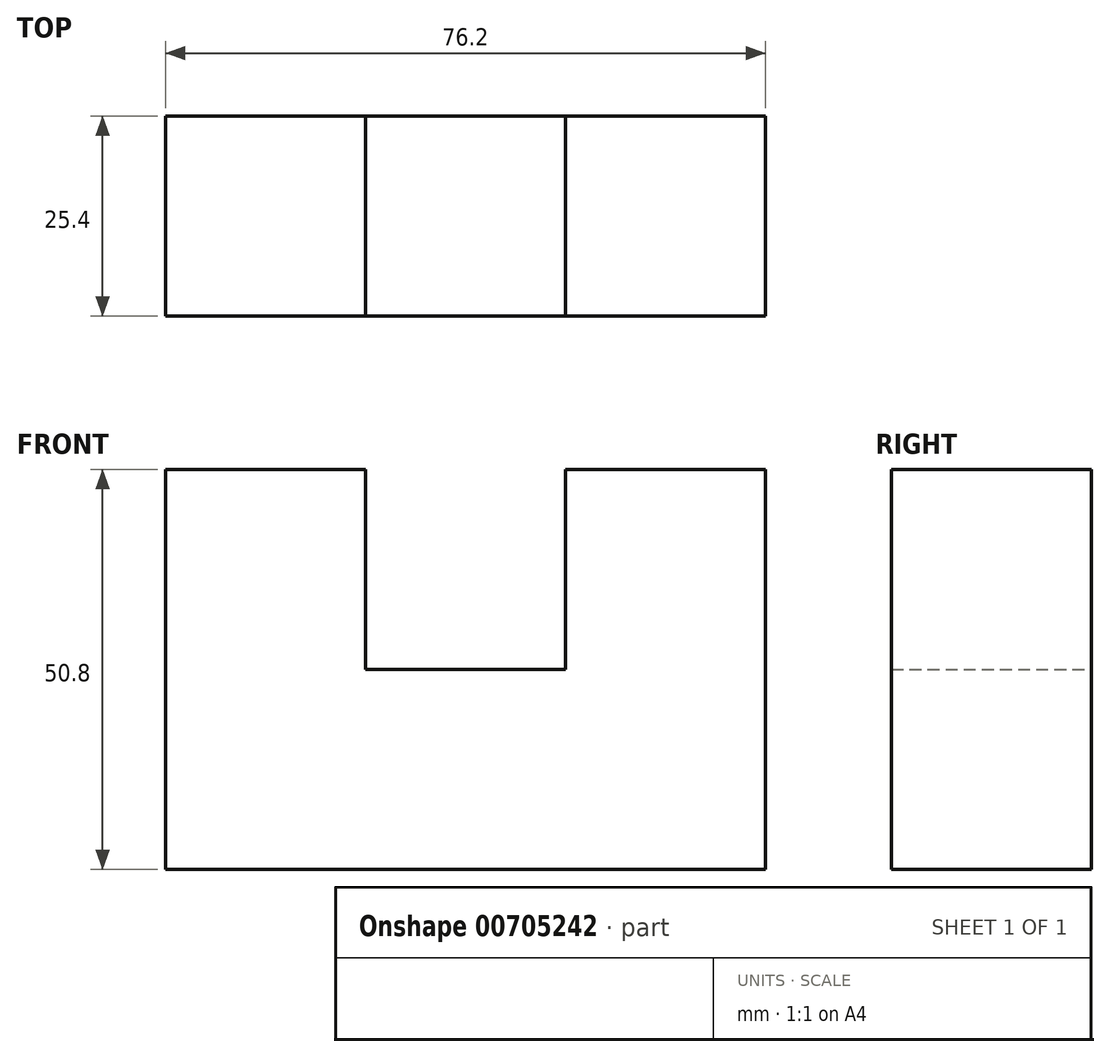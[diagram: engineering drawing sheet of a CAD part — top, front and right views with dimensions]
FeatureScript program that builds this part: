
annotation { "Feature Type Name" : "Feature", "Feature Type Description" : "" }
export const myFeature = defineFeature(function(context is Context, id is Id, definition is map)
    precondition{}
    {
        {
            var Q0;
            Q0=qCreatedBy(makeId("Front.planeOp"),FACE);
            var sketch = newSketch(context, id + "F0", { "sketchPlane" : qUnion([Q0])});
            skLineSegment(sketch, "E0.bottom", {"start": v(0, 0) * mm, "end": v(25.4, 0) * mm});
            skLineSegment(sketch, "E0.top", {"start": v(0, 25.4) * mm, "end": v(25.4, 25.4) * mm});
            skLineSegment(sketch, "E0.left", {"start": v(0, 0) * mm, "end": v(0, 25.4) * mm});
            skLineSegment(sketch, "E0.right", {"start": v(25.4, 0) * mm, "end": v(25.4, 25.4) * mm});
            skLineSegment(sketch, "E1.bottom", {"start": v(0, 25.4) * mm, "end": v(-25.4, 25.4) * mm});
            skLineSegment(sketch, "E1.top", {"start": v(0, 0) * mm, "end": v(-25.4, 0) * mm});
            skLineSegment(sketch, "E1.left", {"start": v(0, 25.4) * mm, "end": v(0, 0) * mm});
            skLineSegment(sketch, "E1.right", {"start": v(-25.4, 25.4) * mm, "end": v(-25.4, 0) * mm});
            skLineSegment(sketch, "E2.bottom", {"start": v(-25.4, 25.4) * mm, "end": v(-50.8, 25.4) * mm});
            skLineSegment(sketch, "E2.top", {"start": v(-25.4, 0) * mm, "end": v(-50.8, 0) * mm});
            skLineSegment(sketch, "E2.right", {"start": v(-50.8, 25.4) * mm, "end": v(-50.8, 0) * mm});
            skLineSegment(sketch, "E3.bottom", {"start": v(-50.8, 25.4) * mm, "end": v(-25.4, 25.4) * mm});
            skLineSegment(sketch, "E3.top", {"start": v(-50.8, 50.8) * mm, "end": v(-25.4, 50.8) * mm});
            skLineSegment(sketch, "E3.left", {"start": v(-50.8, 25.4) * mm, "end": v(-50.8, 50.8) * mm});
            skLineSegment(sketch, "E3.right", {"start": v(-25.4, 25.4) * mm, "end": v(-25.4, 50.8) * mm});
            skLineSegment(sketch, "E4.top", {"start": v(0, 50.8) * mm, "end": v(25.4, 50.8) * mm});
            skLineSegment(sketch, "E4.left", {"start": v(0, 25.4) * mm, "end": v(0, 50.8) * mm});
            skLineSegment(sketch, "E4.right", {"start": v(25.4, 25.4) * mm, "end": v(25.4, 50.8) * mm});
            skSolve(sketch);
        }
        {
            var Q0;
            Q0 = qSketchRegion(id + "F0", true);
            extrude(context, id + "F1", {"entities" : qUnion([Q0]), "depth" : 25.4 * mm, "offsetDistance" : 25.4 * mm});
        }
    });
